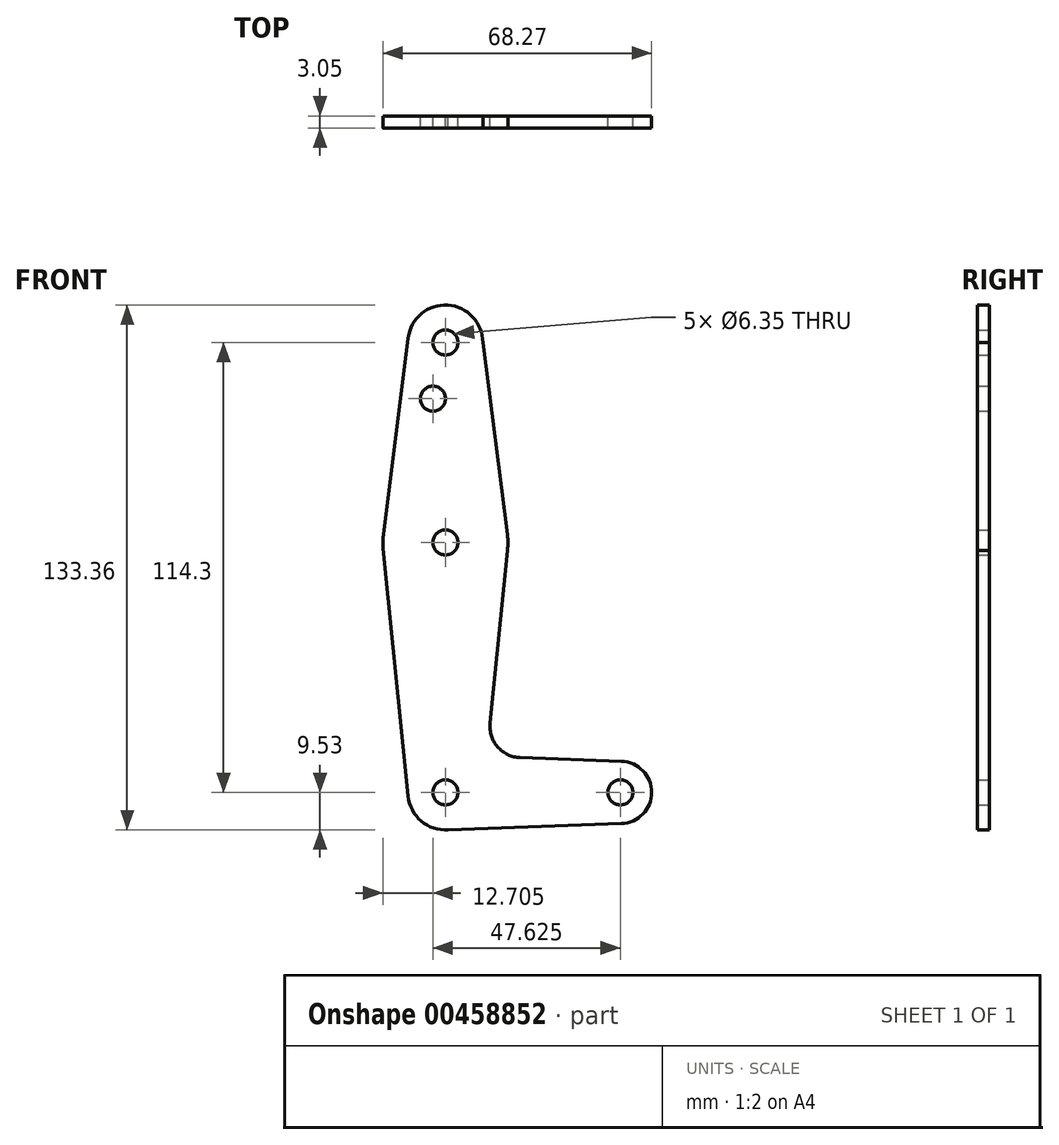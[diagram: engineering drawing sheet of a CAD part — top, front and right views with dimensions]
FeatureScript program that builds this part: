
annotation { "Feature Type Name" : "Feature", "Feature Type Description" : "" }
export const myFeature = defineFeature(function(context is Context, id is Id, definition is map)
    precondition{}
    {
        {
            var Q0;
            Q0=qCreatedBy(makeId("Front.planeOp"),FACE);
            var sketch = newSketch(context, id + "F0", { "sketchPlane" : qUnion([Q0])});
            skCircle(sketch, "E0", {"center": v(0, 0) * mm, "radius": 9.53 * mm});
            skCircle(sketch, "E1", {"center": v(0, 63.5) * mm, "radius": 15.88 * mm});
            skCircle(sketch, "E2", {"center": v(0, 114.3) * mm, "radius": 9.52 * mm});
            skLineSegment(sketch, "E3", {"start": v(0, 114.3) * mm, "end": v(0, 63.5) * mm, "construction": true});
            skLineSegment(sketch, "E4", {"start": v(0, 0) * mm, "end": v(0, 63.5) * mm, "construction": true});
            skCircle(sketch, "E5", {"center": v(44.45, 0) * mm, "radius": 7.94 * mm});
            skLineSegment(sketch, "E6", {"start": v(0, 0) * mm, "end": v(44.45, 0) * mm, "construction": true});
            skLineSegment(sketch, "E7", {"start": v(-9.45, 115.5) * mm, "end": v(-15.75, 65.48) * mm});
            skLineSegment(sketch, "E8", {"start": v(9.52, 114.3) * mm, "end": v(15.75, 65.5) * mm});
            skLineSegment(sketch, "E9", {"start": v(15.75, 61.5) * mm, "end": v(11.34, 17.59) * mm});
            skLineSegment(sketch, "E10", {"start": v(-15.8, 61.91) * mm, "end": v(-9.48, -0.95) * mm});
            skLineSegment(sketch, "E11", {"start": v(0, -9.53) * mm, "end": v(44.73, -7.93) * mm});
            skCircle(sketch, "E12", {"center": v(0, 114.3) * mm, "radius": 3.18 * mm});
            skCircle(sketch, "E13", {"center": v(0, 63.5) * mm, "radius": 3.18 * mm});
            skCircle(sketch, "E14", {"center": v(0, 0) * mm, "radius": 3.18 * mm});
            skCircle(sketch, "E15", {"center": v(44.45, 0) * mm, "radius": 3.18 * mm});
            skCircle(sketch, "E16", {"center": v(-3.17, 100.03) * mm, "radius": 3.18 * mm});
            skLineSegment(sketch, "E17", {"start": v(18.97, 8.85) * mm, "end": v(44.73, 7.93) * mm});
            skArc(sketch, "E18.filletArc", {"start": v(11.34, 17.59) * mm, "mid": v(13.26, 11.57) * mm, "end": v(18.97, 8.85) * mm});
            skSolve(sketch);
        }
        {
            var Q0;
            Q0 = qSketchRegion(id + "F0", true);
            extrude(context, id + "F1", {"entities" : qUnion([Q0]), "depth" : 3.05 * mm});
        }
    });
